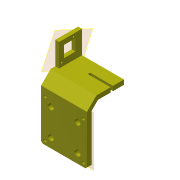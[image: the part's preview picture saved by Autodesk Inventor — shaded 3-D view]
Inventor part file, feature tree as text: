
AUTODESK INVENTOR PART (.ipt)
format: ipt  version: 2022 (Build 260153000, 153)  size: 194,048 bytes
history: native  units: mm
features: other x12, reference x12, sketch x8, extrude x5, plane x3, hole x3
ambient origin geometry x8: Origin, YZ Plane, XZ Plane, XY Plane, X Axis, Y Axis, Z Axis, Center Point
bodies: Solid1 (feature_tree)
feature tree (43):
  plane  "Work Plane1"
  plane  "Work Plane2"
  extrude  "Extrusion1"  Depth=5.0mm
  hole  "Hole1"  [1 undecoded]
  hole  "Hole3"  [1 undecoded]
  sketch  "Skizze13"  dims[d44=135.0deg d45=135.0deg]
  other  "Arbeitspunkt2"
  other  "Arbeitspunkt3"
  extrude  "Extrusion10"  Depth=30.0mm
  plane  "Arbeitsebene4"
  extrude  "Extrusion11"  Depth=15.0mm
  extrude  "Extrusion12"  Depth=5.0mm TaperAngle=0.0deg
  extrude  "Extrusion13"  Depth=3.2mm
  hole  "Bohrung4"  [1 undecoded]
  sketch  "Sketch1"  dims[d0=10.0mm d1=0.0mm]
  reference  "Reference1"
  reference  "Reference4"
  reference  "Reference5"
  sketch  "Sketch2"  dims[d2=4.0mm d3=6.0mm d4=8.0mm d5=4.5mm d6=90.0deg d7=8.0mm d8=20.594885mm]
  reference  "Reference6"
  reference  "Reference7"
  reference  "Reference8"
  reference  "Reference9"
  sketch  "Sketch10"  dims[d30=3.8mm d31=6.0mm d32=8.0mm d33=2.0mm d34=90.0deg d35=20.0mm d36=20.594885mm d43=5.0mm]
  reference  "Reference18"
  reference  "Reference19"
  reference  "Reference20"
  reference  "Reference21"
  reference  "Reference22"
  sketch  "Skizze14"  dims[d46=0.0mm d47=10.0mm d48=0.0mm]
  sketch  "Skizze15"  dims[d49=6.0mm d50=30.0mm]
  sketch  "Skizze16"  dims[d51=30.0mm d52=15.0mm]
  sketch  "Skizze17"  dims[d53=15.0mm d54=5.0mm d55=0.0mm d56=3.2mm d57=0.0mm d58=0.0mm d59=10.0mm d60=0.0mm d61=20.0mm d62=2.8mm d63=6.0mm d64=4.0mm d65=2.0mm d66=90.0deg d67=20.0mm d68=20.594885mm]
  other  "<userpath>\Downloads\cellSTORM\cellSTORM_v5.iam"
  other  "cellSTORM_v5.iam"
  other  "00_XY_stage-CHUO_SEIKI_LD-647-R1:2"
  other  "00_XY_stage-CHUO_SEIKI_LD-647-R1-Bottom:1"
  other  "00_KES400:1"
  other  "00_KES400_Bluray_Lens:1"
  other  "00_XY_stage-CHUO_SEIKI_LD-647-R1:1"
  other  "00_XY_stage-CHUO_SEIKI_LD-647-R1-Top:1"
  other  "<userpath>\Documents\GitHub\cellstorm\INVENTOR\cellSTORM_v6.iam"
  other  "cellSTORM_v6.iam"
note: 3 required parameter values undecoded (feature->parameter linkage not recoverable at this tier; creation-order binding heuristic only, values carry confidence <= 0.55)
